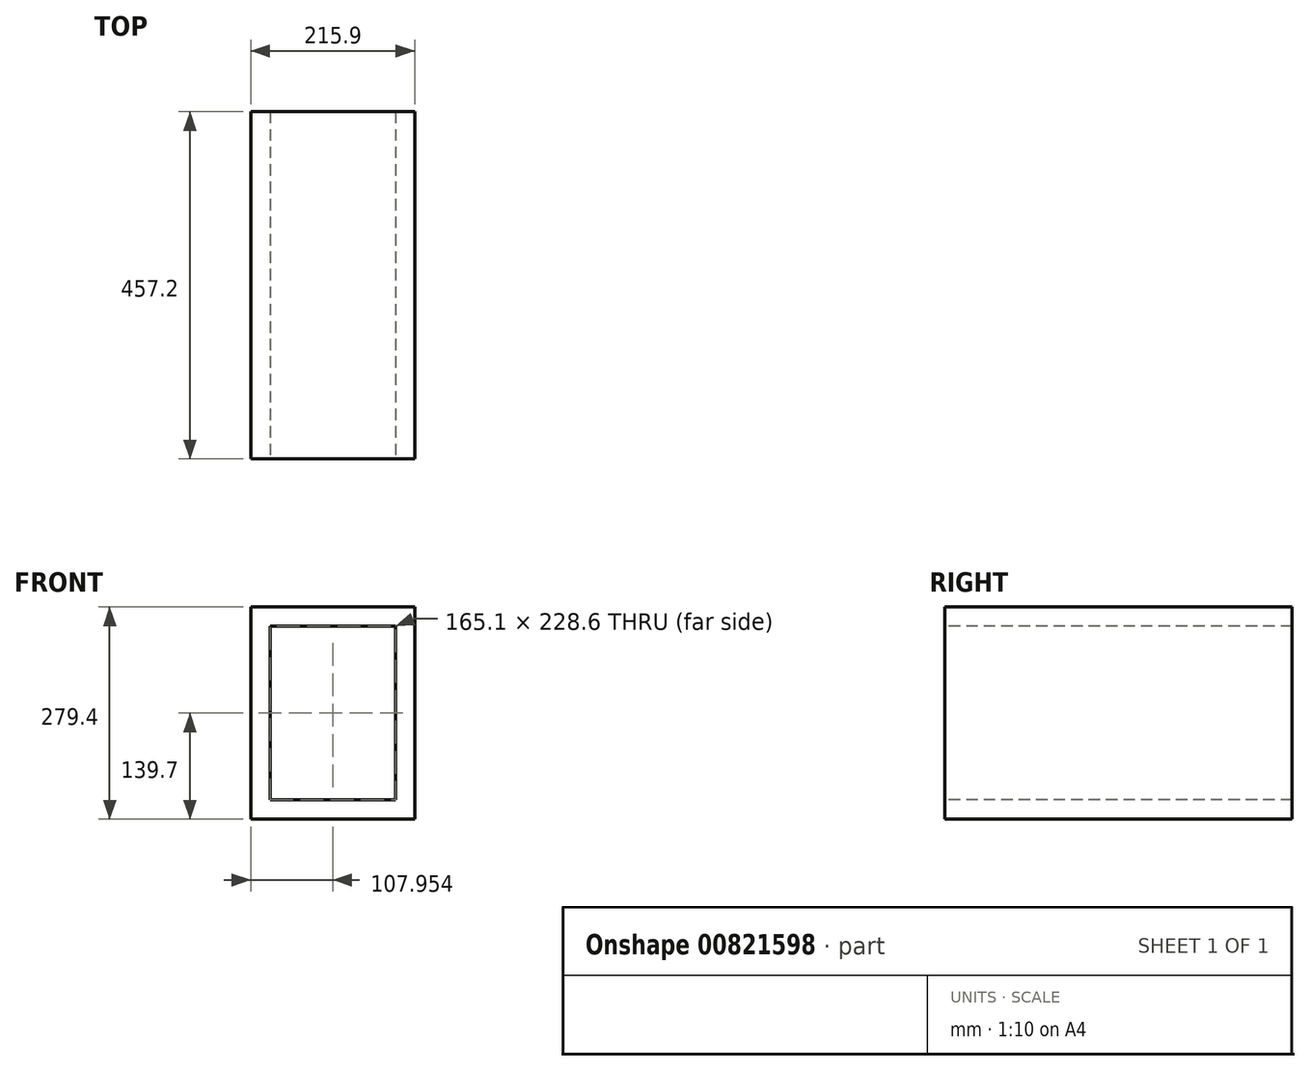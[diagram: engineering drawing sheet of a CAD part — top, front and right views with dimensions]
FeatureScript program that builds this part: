
annotation { "Feature Type Name" : "Feature", "Feature Type Description" : "" }
export const myFeature = defineFeature(function(context is Context, id is Id, definition is map)
    precondition{}
    {
        {
            var Q0;
            Q0=qCreatedBy(makeId("Top.planeOp"),FACE);
            var sketch = newSketch(context, id + "F0", { "sketchPlane" : qUnion([Q0])});
            skLineSegment(sketch, "E0.bottom", {"start": v(-95.94, 393.75) * mm, "end": v(119.96, 393.75) * mm});
            skLineSegment(sketch, "E0.top", {"start": v(-95.94, -63.45) * mm, "end": v(119.96, -63.45) * mm});
            skLineSegment(sketch, "E0.left", {"start": v(-95.94, 393.75) * mm, "end": v(-95.94, -63.45) * mm});
            skLineSegment(sketch, "E0.right", {"start": v(119.96, 393.75) * mm, "end": v(119.96, -63.45) * mm});
            skSolve(sketch);
        }
        {
            var Q0;
            Q0=makeQuery(id+"F0.imprint","IMPRINT",FACE,{"disambiguationData":[TD([[makeQuery(id+"F0.imprint","IMPRINT",EDGE,{"derivedFrom":sQuery(id+"F0.wireOp",EDGE,"E0.bottom")}),-1.0]])]});
            extrude(context, id + "F1", {"entities" : qUnion([Q0]), "endBound" : BoundingType.SYMMETRIC, "depth" : 279.4 * mm, "offsetDistance" : 25.4 * mm});
        }
        {
            var Q0;
            Q0=makeQuery(id+"F1.opExtrude","SWEPT_FACE",FACE,{"disambiguationData":[OSD([sQuery(id+"F0.wireOp",EDGE,"E0.top")])]});
            var sketch = newSketch(context, id + "F2", { "sketchPlane" : qUnion([Q0])});
            skLineSegment(sketch, "E1.bottom", {"start": v(-70.54, 114.3) * mm, "end": v(94.56, 114.3) * mm});
            skLineSegment(sketch, "E1.top", {"start": v(-70.54, -114.3) * mm, "end": v(94.56, -114.3) * mm});
            skLineSegment(sketch, "E1.left", {"start": v(-70.54, 114.3) * mm, "end": v(-70.54, -114.3) * mm});
            skLineSegment(sketch, "E1.right", {"start": v(94.56, 114.3) * mm, "end": v(94.56, -114.3) * mm});
            skSolve(sketch);
        }
        {
            var Q0;
            Q0=makeQuery(id+"F2.imprint","IMPRINT",FACE,{"disambiguationData":[TD([[makeQuery(id+"F2.imprint","IMPRINT",EDGE,{"derivedFrom":sQuery(id+"F2.wireOp",EDGE,"E1.bottom")}),-1.0]])]});
            extrude(context, id + "F3", {"entities" : qUnion([Q0]), "operationType" : NewBodyOperationType.REMOVE, "oppositeDirection" : true, "depth" : 477.52 * mm, "offsetDistance" : 25.4 * mm});
        }
    });
